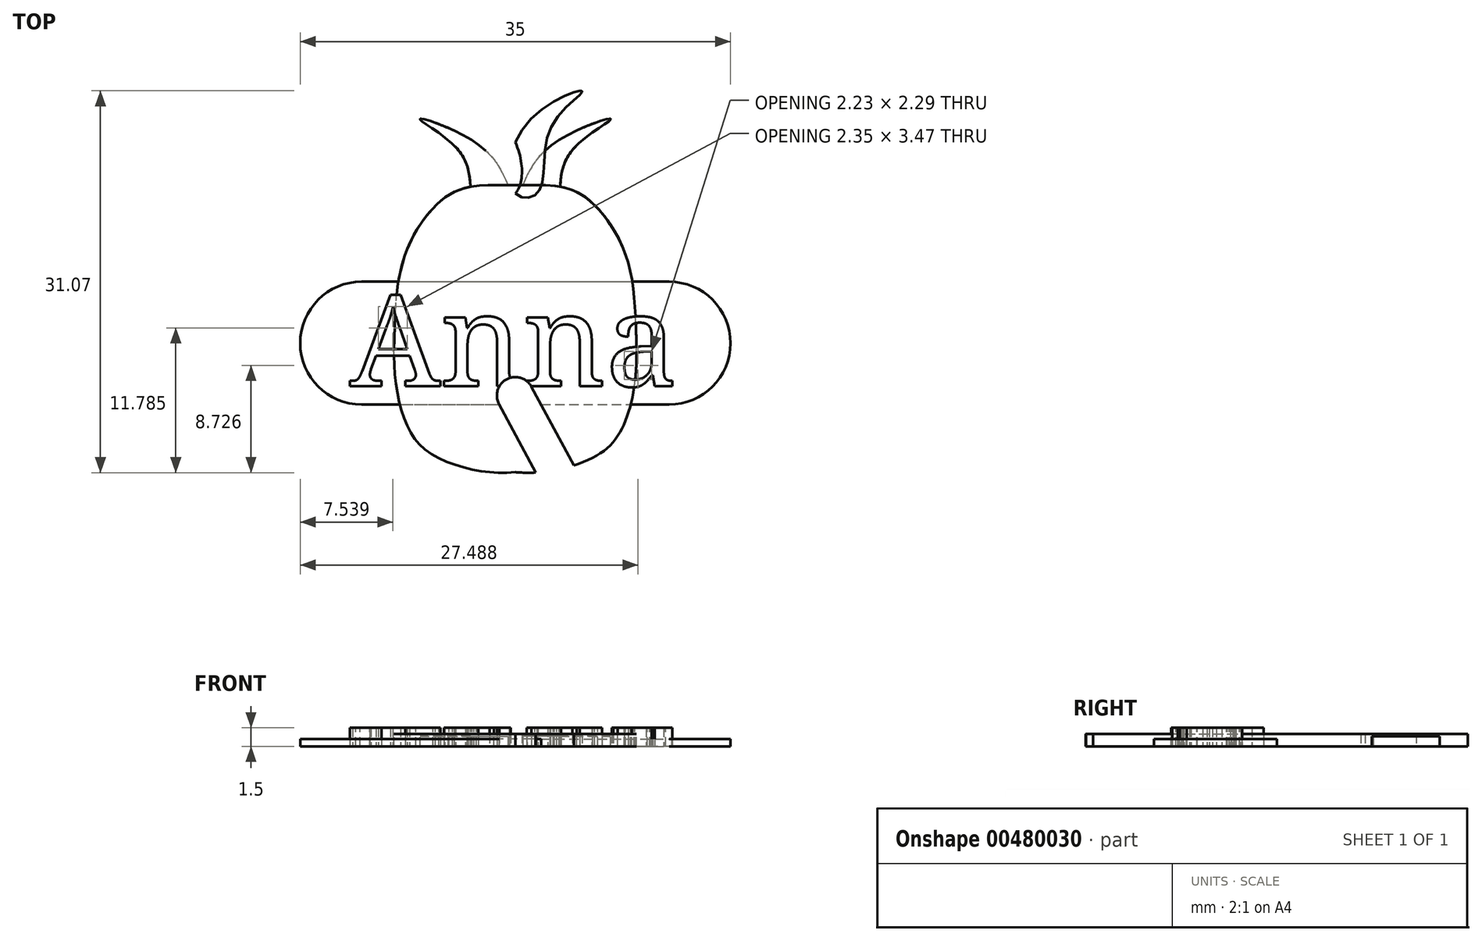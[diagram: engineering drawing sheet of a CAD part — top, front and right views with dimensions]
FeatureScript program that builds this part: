
annotation { "Feature Type Name" : "Feature", "Feature Type Description" : "" }
export const myFeature = defineFeature(function(context is Context, id is Id, definition is map)
    precondition{}
    {
        {
            var Q0;
            Q0=qCreatedBy(makeId("Top.planeOp"),FACE);
            var sketch = newSketch(context, id + "F0", { "sketchPlane" : qUnion([Q0])});
            skText(sketch, "E0", { "text": "Anna", "fontName": "NotoSerif-Regular.ttf"});
            const initialGuessF0  = {"E0": [-0.01344, -0.0075, 1, 0, 0.0075]};
            skSetInitialGuess(sketch, initialGuessF0);
            skSolve(sketch);
        }
        {
            var Q0;
            Q0 = qSketchRegion(id + "F0", true);
            extrude(context, id + "F1", {"entities" : qUnion([Q0]), "depth" : 1.5 * mm, "offsetDistance" : 25 * mm});
        }
        {
            var Q0;
            Q0=qCreatedBy(makeId("Top.planeOp"),FACE);
            var sketch = newSketch(context, id + "F2", { "sketchPlane" : qUnion([Q0])});
            skFitSpline(sketch, "E1", {"points": [v(0, -14.5) * mm, v(-3.65, -14.24) * mm, v(-7.11, -12.83) * mm, v(-8.78, -10.71) * mm, v(-9.74, -7.05) * mm, v(-9.8, -2.69) * mm, v(-9.49, 1.16) * mm, v(-8.52, 4.24) * mm, v(-6.73, 6.94) * mm, v(-4.16, 8.6) * mm, v(0, 8.86) * mm], "startDerivative": vector(-36.01, -3.1) * mm, "endDerivative": vector(39.07, 0.66) * mm});
            skFitSpline(sketch, "E2.MirrorCS", {"points": [v(0, -14.5) * mm, v(3.65, -14.24) * mm, v(7.11, -12.83) * mm, v(8.78, -10.71) * mm, v(9.74, -7.05) * mm, v(9.8, -2.69) * mm, v(9.49, 1.16) * mm, v(8.52, 4.24) * mm, v(6.73, 6.94) * mm, v(4.16, 8.6) * mm, v(0, 8.86) * mm], "startDerivative": vector(36.01, -3.1) * mm, "endDerivative": vector(-39.07, 0.66) * mm});
            skSolve(sketch);
        }
        {
            var Q0;
            Q0=makeQuery(id+"F2.imprint","IMPRINT",FACE,{"disambiguationData":[TD([[makeQuery(id+"F2.imprint","IMPRINT",EDGE,{"derivedFrom":sQuery(id+"F2.wireOp",EDGE,"E1")}),-1.0]])]});
            extrude(context, id + "F3", {"entities" : qUnion([Q0]), "depth" : 1 * mm, "offsetDistance" : 25 * mm});
        }
        {
            var Q0;
            Q0=qCreatedBy(makeId("Top.planeOp"),FACE);
            var sketch = newSketch(context, id + "F4", { "sketchPlane" : qUnion([Q0])});
            skFitSpline(sketch, "E3", {"points": [v(-3.62, 8.13) * mm, v(-4.76, 11.85) * mm, v(-7.76, 14.23) * mm, v(-3.16, 12.26) * mm, v(-0.47, 8.54) * mm], "startDerivative": vector(-0.55, 16.12) * mm, "endDerivative": vector(6.29, -15.12) * mm});
            skLineSegment(sketch, "E4", {"start": v(-3.62, 8.13) * mm, "end": v(-0.47, 8.54) * mm});
            skFitSpline(sketch, "E5.MirrorCS", {"points": [v(3.62, 8.13) * mm, v(4.76, 11.85) * mm, v(7.76, 14.23) * mm, v(3.16, 12.26) * mm, v(0.47, 8.54) * mm], "startDerivative": vector(0.55, 16.12) * mm, "endDerivative": vector(-6.29, -15.12) * mm});
            skLineSegment(sketch, "E6", {"start": v(0.47, 8.54) * mm, "end": v(3.62, 8.13) * mm});
            skSolve(sketch);
        }
        {
            var Q0;
            Q0=makeQuery(id+"F4.imprint","IMPRINT",FACE,{"disambiguationData":[TD([[makeQuery(id+"F4.imprint","IMPRINT",EDGE,{"derivedFrom":sQuery(id+"F4.wireOp",EDGE,"E3")}),-1.0]])]});
            var Q1;
            Q1=makeQuery(id+"F4.imprint","IMPRINT",FACE,{"disambiguationData":[TD([[makeQuery(id+"F4.imprint","IMPRINT",EDGE,{"derivedFrom":sQuery(id+"F4.wireOp",EDGE,"E5.MirrorCS")}),1.0]])]});
            extrude(context, id + "F5", {"entities" : qUnion([Q0, Q1]), "operationType" : NewBodyOperationType.ADD, "depth" : 0.8 * mm, "offsetDistance" : 25 * mm});
        }
        {
            var Q0;
            Q0=qCreatedBy(makeId("Top.planeOp"),FACE);
            var sketch = newSketch(context, id + "F6", { "sketchPlane" : qUnion([Q0])});
            skFitSpline(sketch, "E7", {"points": [v(-1.9, 8.32) * mm, v(-2.9, 13.55) * mm, v(-5.45, 16.5) * mm, v(-0.96, 13.88) * mm, v(0, 8.18) * mm, v(-1.9, 8.32) * mm]});
            skFitSpline(sketch, "E8.MirrorC", {"points": [v(1.9, 8.32) * mm, v(2.9, 13.55) * mm, v(5.45, 16.5) * mm, v(0.96, 13.88) * mm, v(0, 8.18) * mm, v(1.9, 8.32) * mm]});
            skSolve(sketch);
        }
        {
            var Q0;
            {var subQ0=sQuery(id+"F6.wireOp",EDGE,"E8.MirrorC");var subQ1=sQuery(id+"F6.wireOp",EDGE,"E7");var subQ2=makeQuery(id+"F6.imprint","INTERSECT",VERTEX,{"disambiguationData":[OD(0.0)],"derivedFrom":[subQ1,subQ0]});Q0=makeQuery(id+"F6.imprint","IMPRINT",FACE,{"disambiguationData":[TD([[makeQuery(id+"F6.imprint","IMPRINT",EDGE,{"disambiguationData":[TD([[subQ2,-1.0]])],"derivedFrom":subQ1}),-1.0]])]});}
            var Q1;
            {var subQ0=sQuery(id+"F6.wireOp",EDGE,"E8.MirrorC");var subQ1=sQuery(id+"F6.wireOp",EDGE,"E7");var subQ2=makeQuery(id+"F6.imprint","INTERSECT",VERTEX,{"disambiguationData":[OD(0.0)],"derivedFrom":[subQ1,subQ0]});Q1=makeQuery(id+"F6.imprint","IMPRINT",FACE,{"disambiguationData":[TD([[makeQuery(id+"F6.imprint","IMPRINT",EDGE,{"disambiguationData":[TD([[subQ2,1.0]])],"derivedFrom":subQ1}),1.0]])]});}
            extrude(context, id + "F7", {"entities" : qUnion([Q0, Q1]), "depth" : 1 * mm, "offsetDistance" : 25 * mm});
        }
        {
            var Q0;
            Q0=qCreatedBy(makeId("Top.planeOp"),FACE);
            var sketch = newSketch(context, id + "F8", { "sketchPlane" : qUnion([Q0])});
            skLineSegment(sketch, "E9.bottom", {"start": v(-12.5, 1) * mm, "end": v(12.5, 1) * mm});
            skLineSegment(sketch, "E9.top", {"start": v(-12.5, -9) * mm, "end": v(12.5, -9) * mm});
            skArc(sketch, "E10", {"start": v(-12.5, -9) * mm, "mid": v(-17.5, -4) * mm, "end": v(-12.5, 1) * mm});
            skArc(sketch, "E11", {"start": v(12.5, -9) * mm, "mid": v(17.5, -4) * mm, "end": v(12.5, 1) * mm});
            skSolve(sketch);
        }
        {
            var Q0;
            Q0=makeQuery(id+"F8.imprint","IMPRINT",FACE,{"disambiguationData":[TD([[makeQuery(id+"F8.imprint","IMPRINT",EDGE,{"derivedFrom":sQuery(id+"F8.wireOp",EDGE,"E9.bottom")}),-1.0]])]});
            extrude(context, id + "F9", {"entities" : qUnion([Q0]), "depth" : 0.6 * mm, "offsetDistance" : 25 * mm});
        }
        {
            var Q0;
            Q0=qCreatedBy(makeId("Top.planeOp"),FACE);
            var sketch = newSketch(context, id + "F10", { "sketchPlane" : qUnion([Q0])});
            skLineSegment(sketch, "E12", {"start": v(3.92, -18.7) * mm, "end": v(-1.32, -8.97) * mm});
            skLineSegment(sketch, "E13", {"start": v(-1.32, -8.97) * mm, "end": v(1.32, -7.55) * mm, "construction": true});
            skLineSegment(sketch, "E14", {"start": v(1.32, -7.55) * mm, "end": v(6.54, -17.23) * mm});
            skLineSegment(sketch, "E15", {"start": v(6.54, -17.23) * mm, "end": v(3.92, -18.7) * mm});
            skArc(sketch, "E16", {"start": v(-1.32, -8.97) * mm, "mid": v(-0.71, -6.94) * mm, "end": v(1.32, -7.55) * mm});
            skSolve(sketch);
        }
        {
            var Q0;
            Q0=makeQuery(id+"F10.imprint","IMPRINT",FACE,{"disambiguationData":[TD([[makeQuery(id+"F10.imprint","IMPRINT",EDGE,{"derivedFrom":sQuery(id+"F10.wireOp",EDGE,"E12")}),-1.0]])]});
            extrude(context, id + "F11", {"entities" : qUnion([Q0]), "operationType" : NewBodyOperationType.REMOVE, "depth" : 25 * mm, "offsetDistance" : 25 * mm});
        }
    });
